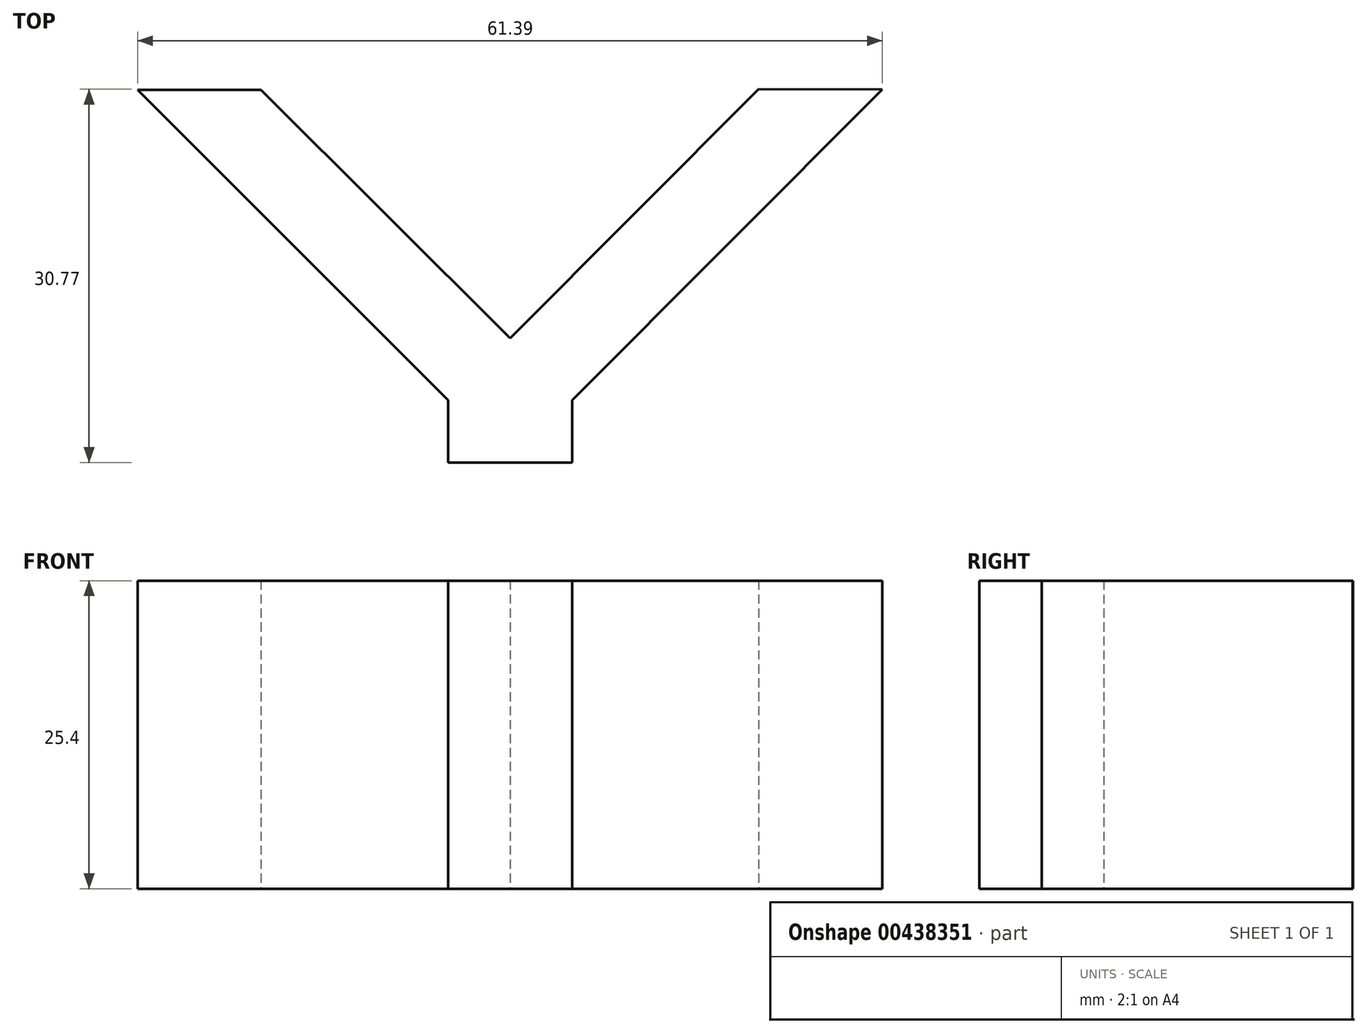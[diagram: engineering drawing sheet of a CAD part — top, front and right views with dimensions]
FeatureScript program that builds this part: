
annotation { "Feature Type Name" : "Feature", "Feature Type Description" : "" }
export const myFeature = defineFeature(function(context is Context, id is Id, definition is map)
    precondition{}
    {
        {
            var Q0;
            Q0=qCreatedBy(makeId("Top.planeOp"),FACE);
            var sketch = newSketch(context, id + "F0", { "sketchPlane" : qUnion([Q0])});
            skLineSegment(sketch, "E0", {"start": v(1.83, 0) * mm, "end": v(22.33, 0) * mm});
            skLineSegment(sketch, "E1", {"start": v(1.83, 0) * mm, "end": v(6.96, 0) * mm});
            skLineSegment(sketch, "E2", {"start": v(22.33, 0) * mm, "end": v(17.2, 0) * mm});
            skLineSegment(sketch, "E3", {"start": v(17.2, 0) * mm, "end": v(17.2, 5.13) * mm});
            skLineSegment(sketch, "E4", {"start": v(17.2, 5.13) * mm, "end": v(22.33, 0) * mm});
            skLineSegment(sketch, "E5", {"start": v(6.96, 0) * mm, "end": v(6.96, 5.13) * mm});
            skLineSegment(sketch, "E6", {"start": v(6.96, 5.13) * mm, "end": v(1.83, 0) * mm});
            skLineSegment(sketch, "E7", {"start": v(6.96, 5.13) * mm, "end": v(17.2, 5.13) * mm});
            skLineSegment(sketch, "E8", {"start": v(12.08, 0) * mm, "end": v(12.08, 10.24) * mm});
            skLineSegment(sketch, "E9", {"start": v(12.08, 10.24) * mm, "end": v(6.96, 5.13) * mm});
            skLineSegment(sketch, "E10", {"start": v(12.08, 10.24) * mm, "end": v(17.2, 5.13) * mm});
            skLineSegment(sketch, "E11", {"start": v(6.96, 5.13) * mm, "end": v(-18.63, 30.72) * mm});
            skLineSegment(sketch, "E12", {"start": v(17.2, 5.13) * mm, "end": v(42.76, 30.76) * mm});
            skLineSegment(sketch, "E13", {"start": v(12.08, 10.24) * mm, "end": v(32.56, 30.77) * mm});
            skLineSegment(sketch, "E14", {"start": v(32.56, 30.77) * mm, "end": v(42.76, 30.76) * mm});
            skLineSegment(sketch, "E15", {"start": v(12.08, 10.24) * mm, "end": v(-8.46, 30.72) * mm});
            skLineSegment(sketch, "E16", {"start": v(-8.46, 30.72) * mm, "end": v(-18.63, 30.72) * mm});
            skSolve(sketch);
        }
        {
            var Q0;
            Q0=makeQuery(id+"F0.imprint","IMPRINT",FACE,{"disambiguationData":[TD([[makeQuery(id+"F0.imprint","IMPRINT",EDGE,{"derivedFrom":sQuery(id+"F0.wireOp",EDGE,"E9")}),-1.0]])]});
            var Q1;
            Q1=makeQuery(id+"F0.imprint","IMPRINT",FACE,{"disambiguationData":[TD([[makeQuery(id+"F0.imprint","IMPRINT",EDGE,{"derivedFrom":sQuery(id+"F0.wireOp",EDGE,"E10")}),1.0]])]});
            var Q2;
            {var subQ0=sQuery(id+"F0.wireOp",EDGE,"E10");Q2=makeQuery(id+"F0.imprint","IMPRINT",FACE,{"disambiguationData":[TD([[makeQuery(id+"F0.imprint","IMPRINT",EDGE,{"derivedFrom":subQ0}),-1.0]])]});}
            var Q3;
            {var subQ0=sQuery(id+"F0.wireOp",EDGE,"E9");Q3=makeQuery(id+"F0.imprint","IMPRINT",FACE,{"disambiguationData":[TD([[makeQuery(id+"F0.imprint","IMPRINT",EDGE,{"derivedFrom":subQ0}),1.0]])]});}
            var Q4;
            Q4=makeQuery(id+"F0.imprint","IMPRINT",FACE,{"disambiguationData":[TD([[makeQuery(id+"F0.imprint","IMPRINT",EDGE,{"derivedFrom":sQuery(id+"F0.wireOp",EDGE,"E1")}),1.0]])]});
            var Q5;
            {var subQ0=sQuery(id+"F0.wireOp",EDGE,"E5");Q5=makeQuery(id+"F0.imprint","IMPRINT",FACE,{"disambiguationData":[TD([[makeQuery(id+"F0.imprint","IMPRINT",EDGE,{"derivedFrom":subQ0}),-1.0]])]});}
            var Q6;
            {var subQ0=sQuery(id+"F0.wireOp",EDGE,"E3");Q6=makeQuery(id+"F0.imprint","IMPRINT",FACE,{"disambiguationData":[TD([[makeQuery(id+"F0.imprint","IMPRINT",EDGE,{"derivedFrom":subQ0}),1.0]])]});}
            var Q7;
            Q7=makeQuery(id+"F0.imprint","IMPRINT",FACE,{"disambiguationData":[TD([[makeQuery(id+"F0.imprint","IMPRINT",EDGE,{"derivedFrom":sQuery(id+"F0.wireOp",EDGE,"E2")}),-1.0]])]});
            extrude(context, id + "F1", {"entities" : qUnion([Q0, Q1, Q2, Q3, Q4, Q5, Q6, Q7]), "depth" : 25.4 * mm});
        }
    });
